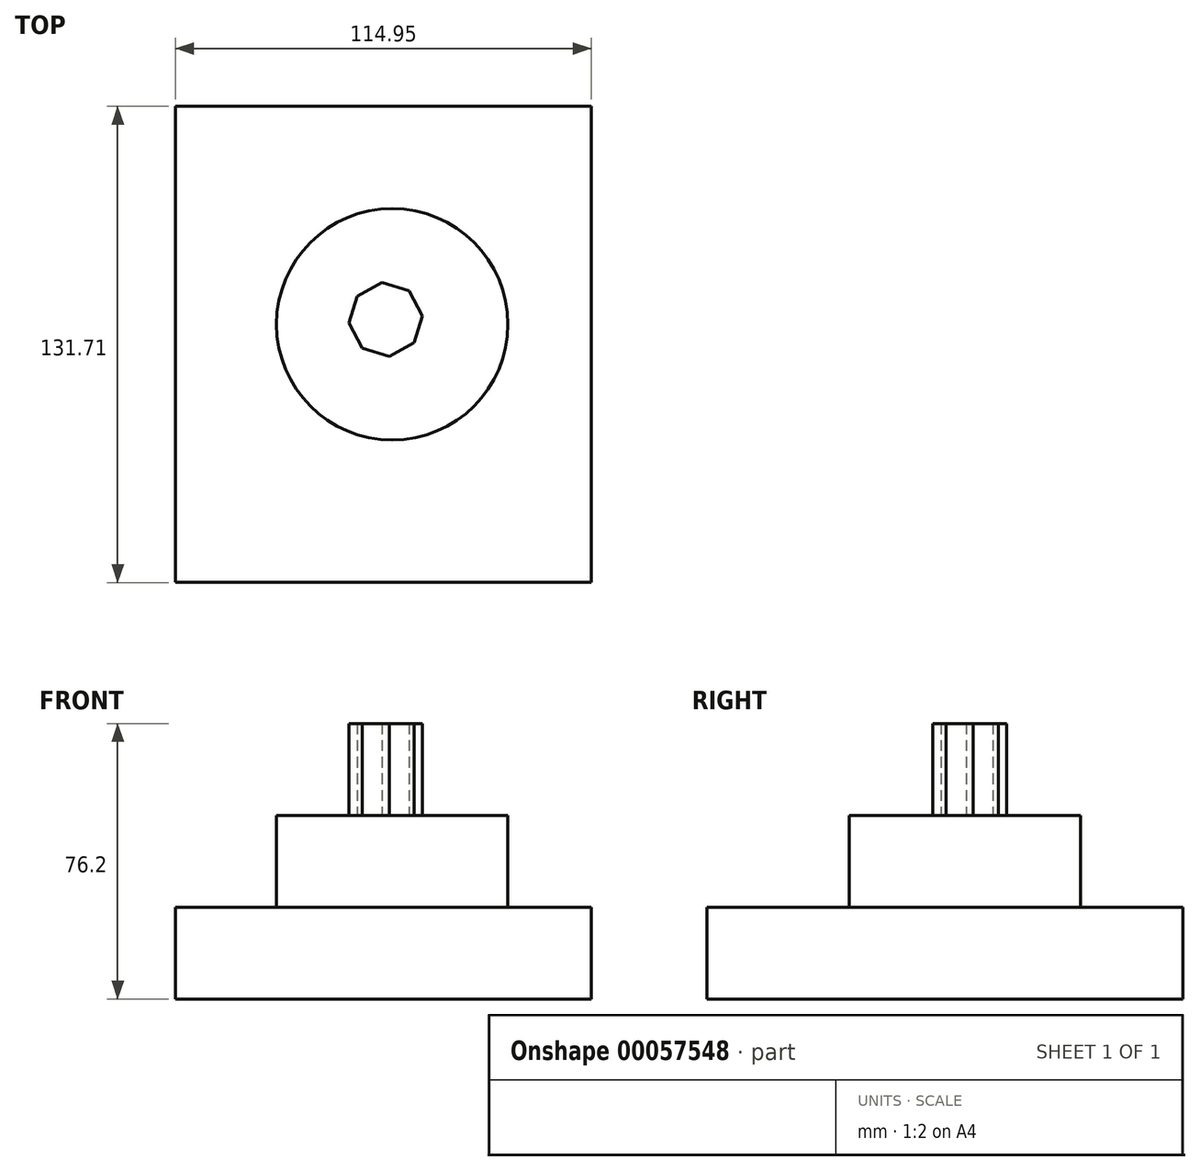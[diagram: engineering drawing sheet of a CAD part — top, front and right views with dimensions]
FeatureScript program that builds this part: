
annotation { "Feature Type Name" : "Feature", "Feature Type Description" : "" }
export const myFeature = defineFeature(function(context is Context, id is Id, definition is map)
    precondition{}
    {
        {
            var Q0;
            Q0=qCreatedBy(makeId("Top.planeOp"),FACE);
            var sketch = newSketch(context, id + "F0", { "sketchPlane" : qUnion([Q0])});
            skLineSegment(sketch, "E0.bottom", {"start": v(-54.5, 54.48) * mm, "end": v(60.46, 54.48) * mm});
            skLineSegment(sketch, "E0.top", {"start": v(-54.5, -77.23) * mm, "end": v(60.46, -77.23) * mm});
            skLineSegment(sketch, "E0.left", {"start": v(-54.5, 54.48) * mm, "end": v(-54.5, -77.23) * mm});
            skLineSegment(sketch, "E0.right", {"start": v(60.46, 54.48) * mm, "end": v(60.46, -77.23) * mm});
            skSolve(sketch);
        }
        {
            var Q0;
            Q0=makeQuery(id+"F0.imprint","IMPRINT",FACE,{"disambiguationData":[TD([[makeQuery(id+"F0.imprint","IMPRINT",EDGE,{"derivedFrom":sQuery(id+"F0.wireOp",EDGE,"E0.bottom")}),-1.0]])]});
            extrude(context, id + "F1", {"entities" : qUnion([Q0]), "depth" : 25.4 * mm});
        }
        {
            var Q0;
            Q0=makeQuery(id+"F1.opExtrude","CAP_FACE",FACE,{"disambiguationData":[OSD([sQuery(id+"F0.wireOp",EDGE,"E0.bottom"),sQuery(id+"F0.wireOp",EDGE,"E0.top"),sQuery(id+"F0.wireOp",EDGE,"E0.left"),sQuery(id+"F0.wireOp",EDGE,"E0.right")])],"isStart":false});
            var sketch = newSketch(context, id + "F2", { "sketchPlane" : qUnion([Q0])});
            skCircle(sketch, "E1", {"center": v(5.44, -5.8) * mm, "radius": 32.02 * mm});
            skSolve(sketch);
        }
        {
            var Q0;
            Q0=makeQuery(id+"F2.imprint","IMPRINT",FACE,{"disambiguationData":[TD([[makeQuery(id+"F2.imprint","IMPRINT",EDGE,{"derivedFrom":sQuery(id+"F2.wireOp",EDGE,"E1")}),1.0]])]});
            extrude(context, id + "F3", {"entities" : qUnion([Q0]), "operationType" : NewBodyOperationType.ADD, "depth" : 25.4 * mm});
        }
        {
            var Q0;
            Q0=makeQuery(id+"F3.opExtrude","CAP_FACE",FACE,{"disambiguationData":[OSD([sQuery(id+"F2.wireOp",EDGE,"E1")])],"isStart":false});
            var sketch = newSketch(context, id + "F4", { "sketchPlane" : qUnion([Q0])});
            skCircle(sketch, "E2.cCircle", {"center": v(3.6, -4.46) * mm, "radius": 9.44 * mm, "construction": true});
            skLineSegment(sketch, "E2.0", {"start": v(10.08, 3.45) * mm, "end": v(13.77, -3.45) * mm});
            skLineSegment(sketch, "E2.1", {"start": v(13.77, -3.45) * mm, "end": v(11.5, -10.93) * mm});
            skLineSegment(sketch, "E2.2", {"start": v(11.5, -10.93) * mm, "end": v(4.62, -14.62) * mm});
            skLineSegment(sketch, "E2.3", {"start": v(4.62, -14.62) * mm, "end": v(-2.87, -12.36) * mm});
            skLineSegment(sketch, "E2.4", {"start": v(-2.87, -12.36) * mm, "end": v(-6.56, -5.47) * mm});
            skLineSegment(sketch, "E2.5", {"start": v(-6.56, -5.47) * mm, "end": v(-4.3, 2.01) * mm});
            skLineSegment(sketch, "E2.6", {"start": v(-4.3, 2.01) * mm, "end": v(2.6, 5.7) * mm});
            skLineSegment(sketch, "E2.7", {"start": v(2.6, 5.7) * mm, "end": v(10.08, 3.45) * mm});
            skPoint(sketch, "E2.0.midPoint", {"position": v(11.92, 0) * mm});
            skSolve(sketch);
        }
        {
            var Q0;
            Q0 = qSketchRegion(id + "F4", true);
            var Q1;
            Q1=makeQuery(id+"F4.imprint","IMPRINT",FACE,{"disambiguationData":[TD([[makeQuery(id+"F4.imprint","IMPRINT",EDGE,{"derivedFrom":sQuery(id+"F4.wireOp",EDGE,"E2.0")}),-1.0]])]});
            extrude(context, id + "F5", {"entities" : qUnion([Q0, Q1]), "operationType" : NewBodyOperationType.ADD, "depth" : 25.4 * mm});
        }
    });
